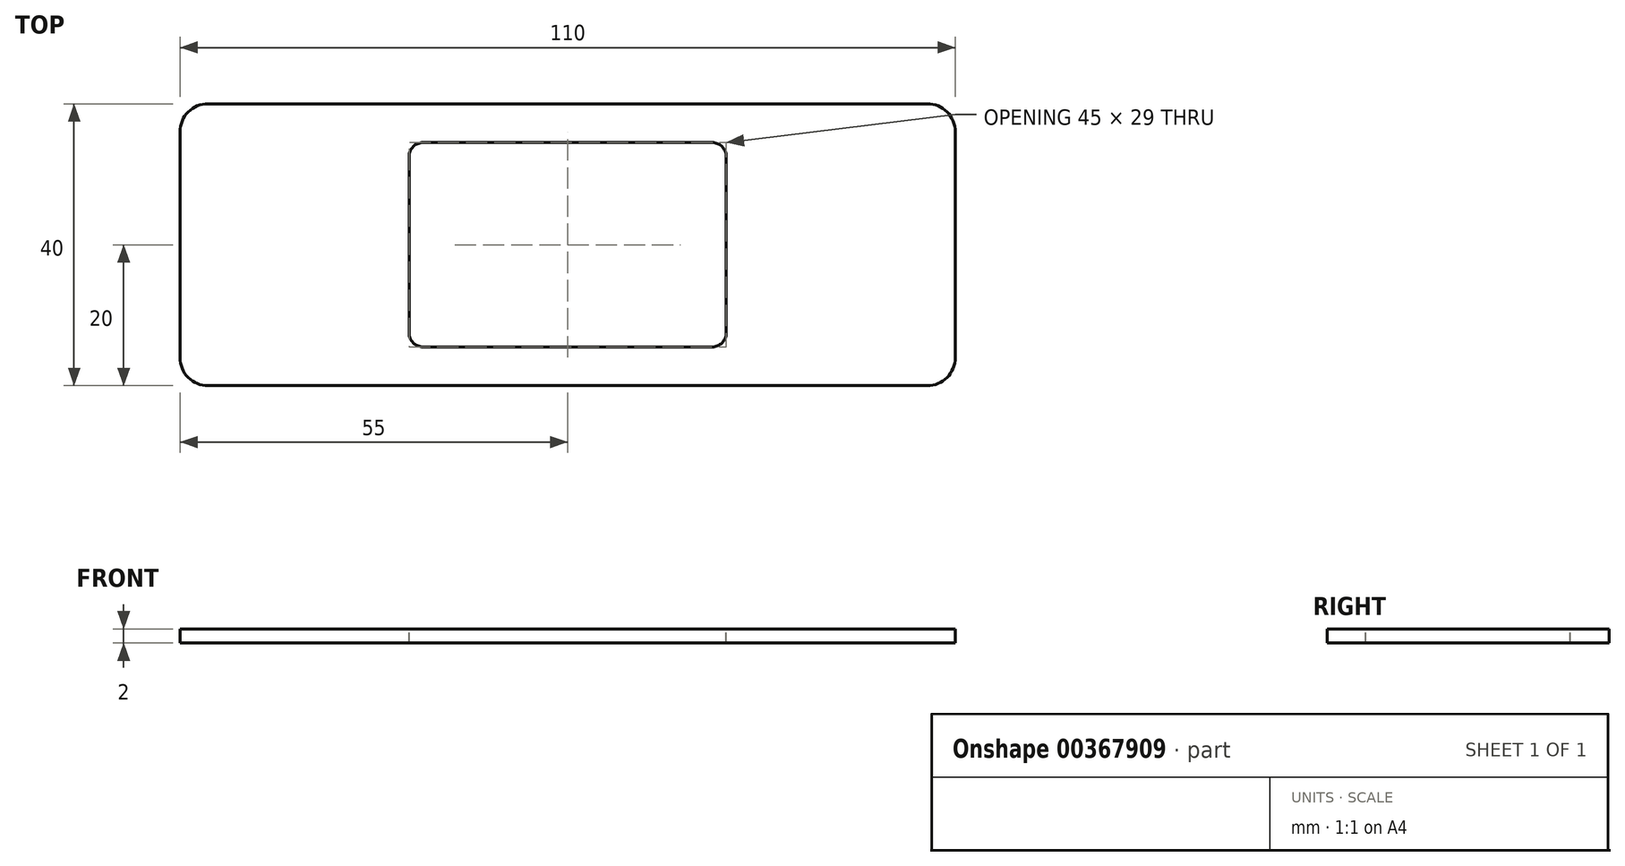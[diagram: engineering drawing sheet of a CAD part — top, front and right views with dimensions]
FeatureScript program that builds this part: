
annotation { "Feature Type Name" : "Feature", "Feature Type Description" : "" }
export const myFeature = defineFeature(function(context is Context, id is Id, definition is map)
    precondition{}
    {
        {
            var Q0;
            Q0=qCreatedBy(makeId("Top.planeOp"),FACE);
            var sketch = newSketch(context, id + "F0", { "sketchPlane" : qUnion([Q0])});
            skLineSegment(sketch, "E0.bottom", {"start": v(-55, 20) * mm, "end": v(55, 20) * mm});
            skLineSegment(sketch, "E0.top", {"start": v(-55, -20) * mm, "end": v(55, -20) * mm});
            skLineSegment(sketch, "E0.left", {"start": v(-55, 20) * mm, "end": v(-55, -20) * mm});
            skLineSegment(sketch, "E0.right", {"start": v(55, 20) * mm, "end": v(55, -20) * mm});
            skPoint(sketch, "E0.middle", {"position": v(0, 0) * mm});
            skSolve(sketch);
        }
        {
            var Q0;
            Q0=makeQuery(id+"F0.imprint","IMPRINT",FACE,{"disambiguationData":[TD([[makeQuery(id+"F0.imprint","IMPRINT",EDGE,{"derivedFrom":sQuery(id+"F0.wireOp",EDGE,"E0.bottom")}),-1.0]])]});
            extrude(context, id + "F1", {"entities" : qUnion([Q0]), "depth" : 2 * mm});
        }
        {
            var Q0;
            Q0=makeQuery(id+"F1.opExtrude","CAP_FACE",FACE,{"disambiguationData":[OSD([sQuery(id+"F0.wireOp",EDGE,"E0.bottom"),sQuery(id+"F0.wireOp",EDGE,"E0.top"),sQuery(id+"F0.wireOp",EDGE,"E0.left"),sQuery(id+"F0.wireOp",EDGE,"E0.right")])],"isStart":false});
            var sketch = newSketch(context, id + "F2", { "sketchPlane" : qUnion([Q0])});
            skLineSegment(sketch, "E1.bottom", {"start": v(22.5, 14.5) * mm, "end": v(-22.5, 14.5) * mm});
            skLineSegment(sketch, "E1.top", {"start": v(22.5, -14.5) * mm, "end": v(-22.5, -14.5) * mm});
            skLineSegment(sketch, "E1.left", {"start": v(22.5, 14.5) * mm, "end": v(22.5, -14.5) * mm});
            skLineSegment(sketch, "E1.right", {"start": v(-22.5, 14.5) * mm, "end": v(-22.5, -14.5) * mm});
            skPoint(sketch, "E1.middle", {"position": v(0, 0) * mm});
            skSolve(sketch);
        }
        {
            var Q0;
            Q0=makeQuery(id+"F2.imprint","IMPRINT",FACE,{"disambiguationData":[TD([[makeQuery(id+"F2.imprint","IMPRINT",EDGE,{"derivedFrom":sQuery(id+"F2.wireOp",EDGE,"E1.bottom")}),1.0]])]});
            extrude(context, id + "F3", {"entities" : qUnion([Q0]), "operationType" : NewBodyOperationType.REMOVE, "endBound" : BoundingType.THROUGH_ALL, "oppositeDirection" : true, "depth" : 25 * mm});
        }
        {
            var Q0;
            Q0=makeQuery(id+"F3.boolean.opBoolean","COPY",EDGE,{"derivedFrom":makeQuery(id+"F3.opExtrude","SWEPT_EDGE",EDGE,{"disambiguationData":[OSD([sQuery(id+"F2.wireOp",EDGE,"E1.bottom"),sQuery(id+"F2.wireOp",EDGE,"E1.right")])]})});
            var Q1;
            Q1=makeQuery(id+"F3.boolean.opBoolean","COPY",EDGE,{"derivedFrom":makeQuery(id+"F3.opExtrude","SWEPT_EDGE",EDGE,{"disambiguationData":[OSD([sQuery(id+"F2.wireOp",EDGE,"E1.bottom"),sQuery(id+"F2.wireOp",EDGE,"E1.left")])]})});
            var Q2;
            Q2=makeQuery(id+"F3.boolean.opBoolean","COPY",EDGE,{"derivedFrom":makeQuery(id+"F3.opExtrude","SWEPT_EDGE",EDGE,{"disambiguationData":[OSD([sQuery(id+"F2.wireOp",EDGE,"E1.top"),sQuery(id+"F2.wireOp",EDGE,"E1.right")])]})});
            var Q3;
            Q3=makeQuery(id+"F3.boolean.opBoolean","COPY",EDGE,{"derivedFrom":makeQuery(id+"F3.opExtrude","SWEPT_EDGE",EDGE,{"disambiguationData":[OSD([sQuery(id+"F2.wireOp",EDGE,"E1.top"),sQuery(id+"F2.wireOp",EDGE,"E1.left")])]})});
            fillet(context, id + "F4", {"entities" : qUnion([Q0, Q1, Q2, Q3]), "radius" : 2 * mm, "tangentPropagation" : true, "allowEdgeOverflow" : false});
        }
        {
            var Q0;
            Q0=makeQuery(id+"F1.opExtrude","SWEPT_EDGE",EDGE,{"disambiguationData":[OSD([sQuery(id+"F0.wireOp",EDGE,"E0.top"),sQuery(id+"F0.wireOp",EDGE,"E0.left")])]});
            var Q1;
            Q1=makeQuery(id+"F1.opExtrude","SWEPT_EDGE",EDGE,{"disambiguationData":[OSD([sQuery(id+"F0.wireOp",EDGE,"E0.bottom"),sQuery(id+"F0.wireOp",EDGE,"E0.left")])]});
            var Q2;
            Q2=makeQuery(id+"F1.opExtrude","SWEPT_EDGE",EDGE,{"disambiguationData":[OSD([sQuery(id+"F0.wireOp",EDGE,"E0.bottom"),sQuery(id+"F0.wireOp",EDGE,"E0.right")])]});
            var Q3;
            Q3=makeQuery(id+"F1.opExtrude","SWEPT_EDGE",EDGE,{"disambiguationData":[OSD([sQuery(id+"F0.wireOp",EDGE,"E0.top"),sQuery(id+"F0.wireOp",EDGE,"E0.right")])]});
            fillet(context, id + "F5", {"entities" : qUnion([Q0, Q1, Q2, Q3]), "radius" : 4 * mm, "tangentPropagation" : true, "allowEdgeOverflow" : false});
        }
    });
